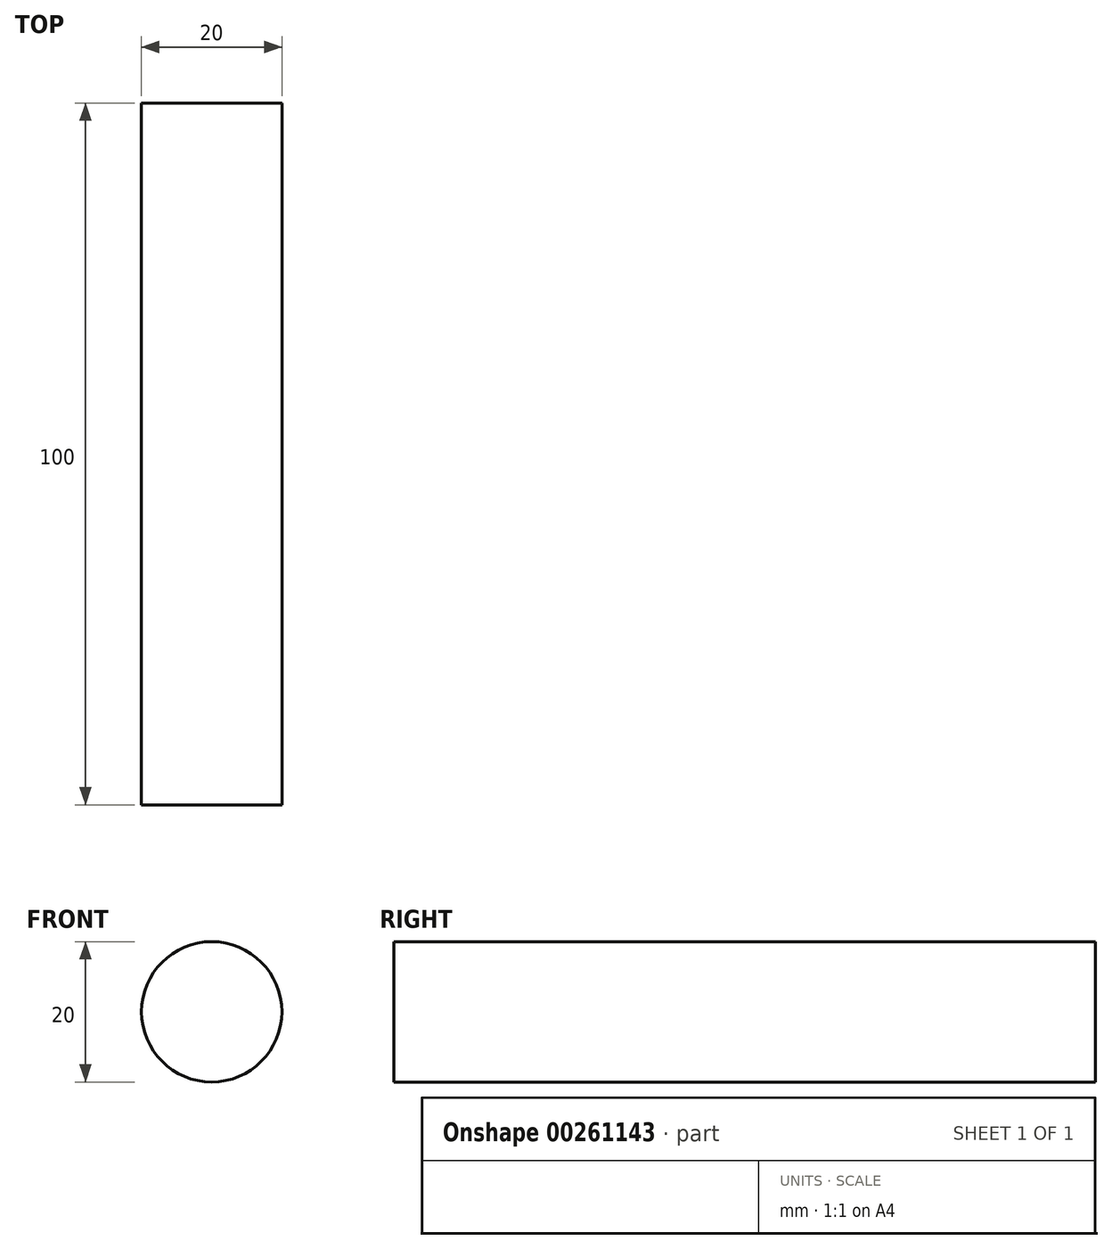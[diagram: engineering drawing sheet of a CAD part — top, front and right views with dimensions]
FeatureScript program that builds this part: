
annotation { "Feature Type Name" : "Feature", "Feature Type Description" : "" }
export const myFeature = defineFeature(function(context is Context, id is Id, definition is map)
    precondition{}
    {
        {
            var Q0;
            Q0=qCreatedBy(makeId("Front.planeOp"),FACE);
            var sketch = newSketch(context, id + "F0", { "sketchPlane" : qUnion([Q0])});
            skCircle(sketch, "E0", {"center": v(0, 0) * mm, "radius": 10 * mm});
            skSolve(sketch);
        }
        {
            var Q0;
            Q0=makeQuery(id+"F0.imprint","IMPRINT",FACE,{"disambiguationData":[TD([[makeQuery(id+"F0.imprint","IMPRINT",EDGE,{"derivedFrom":sQuery(id+"F0.wireOp",EDGE,"E0")}),1.0]])]});
            extrude(context, id + "F1", {"entities" : qUnion([Q0]), "depth" : 100 * mm});
        }
    });
